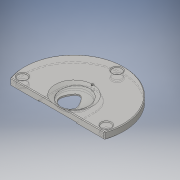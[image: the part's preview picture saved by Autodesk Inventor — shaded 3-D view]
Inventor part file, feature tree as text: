
AUTODESK INVENTOR PART (.ipt)
format: ipt  version: 2016 (Build 200138000, 138)  size: 272,384 bytes
history: native  units: in
note: dims shown in document units (in); Inventor stores cm internally (conversion verified against a paired STEP export)
features: chamfer x15, sketch x6, other x5, extrude x5, hole x3, projected_geometry x1
ambient origin geometry x8: Origin, YZ Plane, XZ Plane, XY Plane, X Axis, Y Axis, Z Axis, Center Point
bodies: Solid1 (feature_tree)
feature tree (35):
  other  "Bottom Plane for Slope"
  other  "Bottom Plane"
  other  "Top Plane for Slope"
  other  "Top Plane"
  other  "Slope Plane"
  extrude  "Main Platform"  Depth=0.0787in
  extrude  "Main Hole"  Depth=0.1969in TaperAngle=0.0deg
  extrude  "Window Recess"  Depth=0.1969in
  hole  "Window Removal Holes"  [1 undecoded]
  extrude  "Slope"  Depth=0.0787in
  sketch  "Sketch14"  dims[d8=0.1969in d9=0.3436in]
  chamfer  "Chamfer1"  Distance=0.1969in
  extrude  "Extrusion6"  Depth=0.0591in
  hole  "Top Magnet Holes"  [1 undecoded]
  hole  "Bottom Magnet Holes"  [1 undecoded]
  chamfer  "Chamfer7"  Distance=2.0in
  chamfer  "Chamfer8"  Distance=2.0in
  chamfer  "Chamfer9"  Distance=0.0394in
  chamfer  "Chamfer10"  Distance=0.0787in Angle=60.0deg
  chamfer  "Chamfer11"  Distance=0.0197in Angle=45.0deg
  chamfer  "Chamfer12"  Distance=0.0197in Angle=45.0deg
  chamfer  "Chamfer13"  Distance=0.1718in
  chamfer  "Chamfer14"  Distance=0.1718in
  chamfer  "Chamfer15"  Distance=1.0in
  chamfer  "Chamfer16"  Distance=0.0197in Angle=45.0deg
  chamfer  "Chamfer17"  Distance=0.0197in Angle=45.0deg
  chamfer  "Chamfer18"  Distance=0.0197in Angle=45.0deg
  chamfer  "Chamfer19"  Distance=0.0197in Angle=45.0deg
  chamfer  "Chamfer20"  Distance=0.0197in Angle=45.0deg
  sketch  "Sketch3"  dims[d0=2.8346in d1=0.0787in]
  sketch  "Sketch4"  dims[d2=0.7874in d3=0.1969in d4=0.0in]
  sketch  "Sketch5"  dims[d6=1.0787in d7=0.1969in]
  sketch  "Sketch15"  dims[d10=0.3436in d11=0.0787in d12=0.1969in d13=0.0in]
  sketch  "Sketch17"  dims[d14=0.0394in d15=0.0in d16=0.0591in d17=0.75in d18=0.375in d19=0.25in d20=0.5635in d21=1.0in d22=0.8108in d24=0.0591in d25=0.1181in d26=2.0in d27=2.0in d28=2.0in d29=2.0in d30=0.0394in d31=0.0in d42=0.2559in d43=0.75in d44=0.375in d45=0.25in d46=0.5635in d47=0.0197in d48=0.0in d49=0.2559in d50=0.75in d51=0.375in d52=0.25in d53=0.5635in d54=0.0591in d55=0.0in d56=0.0787in d57=0.125in d58=60.0deg d74=0.0197in d75=0.125in d76=45.0deg d77=0.0197in d78=0.125in d79=45.0deg d81=0.1718in d82=0.1718in d83=1.0in d84=0.0in d85=0.0197in d86=0.125in d87=45.0deg d88=0.0197in d89=0.125in d90=45.0deg d91=0.0197in d92=0.125in d93=45.0deg d94=0.0197in d95=0.125in d96=45.0deg d97=0.0197in d98=0.125in d99=45.0deg d100=0.0197in d101=0.125in d102=45.0deg d103=0.0197in d104=0.125in d105=45.0deg d106=0.0197in d107=0.125in d108=45.0deg d109=0.0197in d110=0.125in d111=45.0deg d112=0.0197in d113=0.125in d114=45.0deg d115=0.0197in d116=0.125in d117=45.0deg d118=0.0197in d119=0.125in d120=45.0deg]
  projected_geometry  "Projected Loop7"
note: 3 required parameter values undecoded (feature->parameter linkage not recoverable at this tier; creation-order binding heuristic only, values carry confidence <= 0.55)
